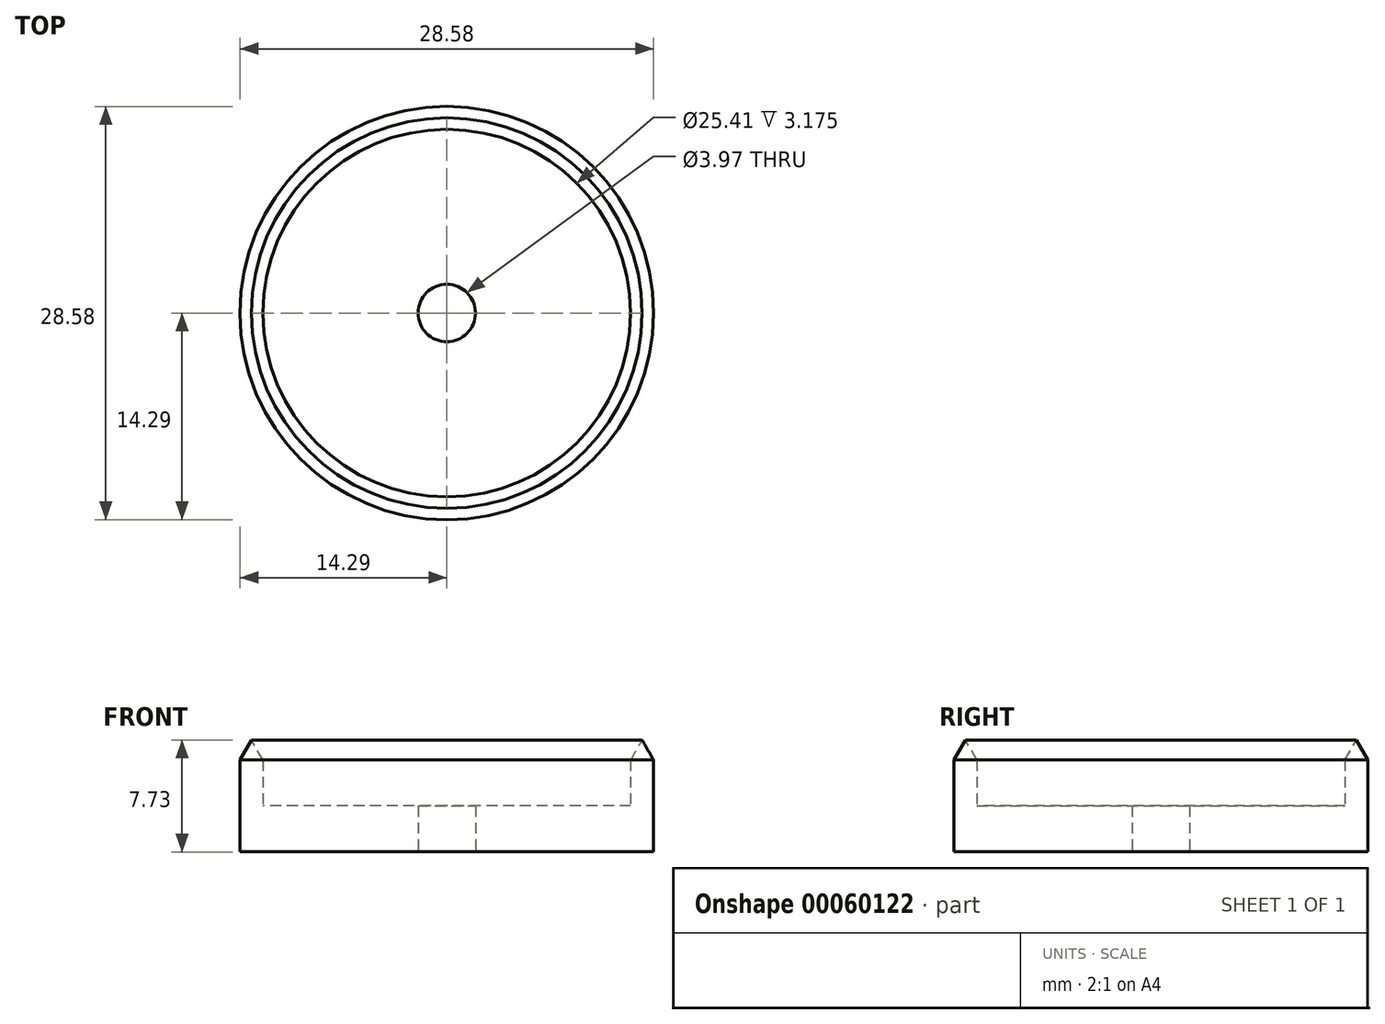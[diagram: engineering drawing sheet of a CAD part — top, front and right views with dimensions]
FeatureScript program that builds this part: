
annotation { "Feature Type Name" : "Feature", "Feature Type Description" : "" }
export const myFeature = defineFeature(function(context is Context, id is Id, definition is map)
    precondition{}
    {
        {
            var Q0;
            Q0=qCreatedBy(makeId("Front.planeOp"),FACE);
            var sketch = newSketch(context, id + "F0", { "sketchPlane" : qUnion([Q0])});
            skLineSegment(sketch, "E0", {"start": v(14.3, -3.17) * mm, "end": v(13.5, -4.55) * mm});
            skLineSegment(sketch, "E1", {"start": v(13.5, -4.55) * mm, "end": v(12.7, -3.17) * mm});
            skLineSegment(sketch, "E2", {"start": v(0, 22.22) * mm, "end": v(0, 22.22) * mm});
            skLineSegment(sketch, "E3", {"start": v(0, 70.97) * mm, "end": v(0, -90.92) * mm, "construction": true});
            skLineSegment(sketch, "E4", {"start": v(0, 22.22) * mm, "end": v(14.3, 22.22) * mm, "construction": true});
            skLineSegment(sketch, "E5", {"start": v(12.7, -3.18) * mm, "end": v(12.7, 0) * mm});
            skLineSegment(sketch, "E6", {"start": v(14.3, -3.18) * mm, "end": v(14.3, 0) * mm});
            skLineSegment(sketch, "E7", {"start": v(12.7, 0) * mm, "end": v(0, 0) * mm});
            skLineSegment(sketch, "E8", {"start": v(0, 3.17) * mm, "end": v(14.3, 3.17) * mm});
            skLineSegment(sketch, "E9", {"start": v(14.3, 3.18) * mm, "end": v(14.3, 0) * mm});
            skLineSegment(sketch, "E10.MirrorCS", {"start": v(-13.5, -4.55) * mm, "end": v(-12.7, -3.18) * mm, "construction": true});
            skLineSegment(sketch, "E11.MirrorCS", {"start": v(-14.3, -3.18) * mm, "end": v(-14.3, 0) * mm, "construction": true});
            skLineSegment(sketch, "E12.MirrorCS", {"start": v(-14.3, -3.18) * mm, "end": v(-13.5, -4.55) * mm, "construction": true});
            skLineSegment(sketch, "E13.MirrorCS", {"start": v(-12.7, -3.18) * mm, "end": v(-12.7, 0) * mm, "construction": true});
            skLineSegment(sketch, "E14.MirrorCS", {"start": v(-14.3, 3.17) * mm, "end": v(-14.3, 0) * mm, "construction": true});
            skLineSegment(sketch, "E15.MirrorCS", {"start": v(0, 3.17) * mm, "end": v(-14.3, 3.17) * mm, "construction": true});
            skLineSegment(sketch, "E16.MirrorCS", {"start": v(-12.7, 0) * mm, "end": v(0, 0) * mm, "construction": true});
            skLineSegment(sketch, "E17", {"start": v(0, 3.17) * mm, "end": v(0, 0) * mm});
            skSolve(sketch);
        }
        {
            var Q0;
            Q0=makeQuery(id+"F0.imprint","IMPRINT",FACE,{"disambiguationData":[TD([[makeQuery(id+"F0.imprint","IMPRINT",EDGE,{"derivedFrom":sQuery(id+"F0.wireOp",EDGE,"E5")}),-1.0]])]});
            var Q1;
            Q1=sQuery(id+"F0.wireOp",EDGE,"E3");
            revolve(context, id + "F1", {"entities" : qUnion([Q0]), "axis" : qUnion([Q1]), "revolveType" : RevolveType.FULL});
        }
        {
            var Q0;
            Q0=makeQuery(id+"F1.opRevolve","SWEPT_FACE",FACE,{"disambiguationData":[OSD([sQuery(id+"F0.wireOp",EDGE,"E8")])]});
            var sketch = newSketch(context, id + "F2", { "sketchPlane" : qUnion([Q0])});
            skCircle(sketch, "E18", {"center": v(0, 0) * mm, "radius": 1.98 * mm});
            skSolve(sketch);
        }
        {
            var Q0;
            Q0=makeQuery(id+"F2.imprint","IMPRINT",FACE,{"disambiguationData":[TD([[makeQuery(id+"F2.imprint","IMPRINT",EDGE,{"derivedFrom":sQuery(id+"F2.wireOp",EDGE,"E18")}),1.0]])]});
            extrude(context, id + "F3", {"entities" : qUnion([Q0]), "operationType" : NewBodyOperationType.REMOVE, "endBound" : BoundingType.THROUGH_ALL, "oppositeDirection" : true, "depth" : 25.4 * mm});
        }
        {
            var Q0;
            Q0=makeQuery(id+"F1.opRevolve","SWEPT_BODY",BODY,{"disambiguationData":[OSD([sQuery(id+"F0.wireOp",EDGE,"E5"),sQuery(id+"F0.wireOp",EDGE,"E0"),sQuery(id+"F0.wireOp",EDGE,"E7"),sQuery(id+"F0.wireOp",EDGE,"E6"),sQuery(id+"F0.wireOp",EDGE,"E8"),sQuery(id+"F0.wireOp",EDGE,"E1"),sQuery(id+"F0.wireOp",EDGE,"E9"),sQuery(id+"F0.wireOp",EDGE,"E17")])]});
            var Q1;
            Q1=sQuery(id+"F0.wireOp",EDGE,"E16.MirrorCS");
            transform(context, id + "F4", {"entities" : qUnion([Q0]), "transformType" : TransformType.ROTATION, "transformAxis" : qUnion([Q1]), "angle" : 180 * degree, "makeCopy" : false});
        }
    });
